# Revit family: SNS GDPX +
name_source: partatom
category: Electrical Equipment
units: mm (PartAtom-declared; Revit-internal decimal feet)

## family parameters
Always vertical = Yes
Cut with Voids When Loaded = No
OmniClass Number = 23.80.30.11.17
OmniClass Title = Distribution Boards and Control Panels
Part Type = Other Panel
Room Calculation Point = No
Round Connector Dimension = Use Diameter
Shared = No
Work Plane-Based = No

## types (1)
- SNS GDPX+
    Default Height = 4' - 0"
    Description = The Merlin GDPX+ is a 16 zone gas pressure proving & detection panel which can be used in many applications, e.g. mechanical rooms, car parks, shopping malls and the most common being a boiler house application
    Load = 120 VA
    Manufacturer = S&S Northern Ltd.
    Model = SNS Merlin Merlin GDPX+
    Product Information = https://snsnorthern.com
    Type Comments = The Merlin GDPX+ is a 16 zone gas pressure proving & detection panel which can be used in many applications, e.g. mechanical rooms, car parks, shopping malls and the most common being a boiler house application
    URL = https://snsnorthern.com
    Voltage = 120VAC

## geometry (parser evidence)
native form markers: Blend x4, Sweep x11
no freeform markers — native parametric forms only
